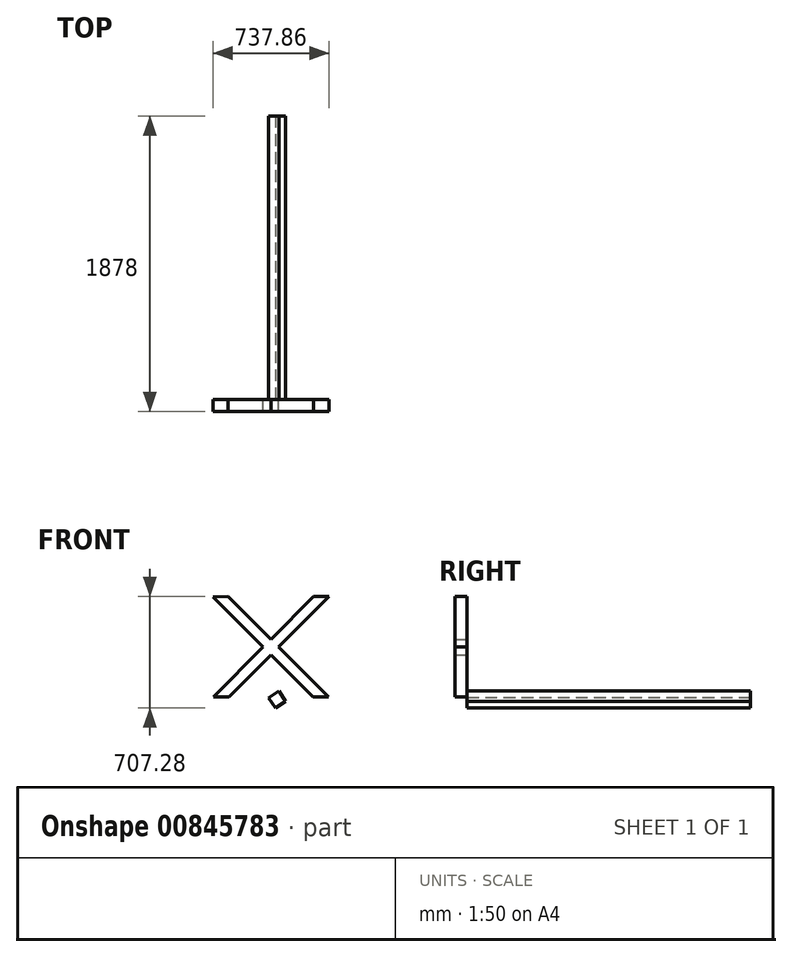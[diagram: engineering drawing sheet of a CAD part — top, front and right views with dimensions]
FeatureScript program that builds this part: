
annotation { "Feature Type Name" : "Feature", "Feature Type Description" : "" }
export const myFeature = defineFeature(function(context is Context, id is Id, definition is map)
    precondition{}
    {
        {
            var Q0;
            Q0=qCreatedBy(makeId("Front.planeOp"),FACE);
            var sketch = newSketch(context, id + "F0", { "sketchPlane" : qUnion([Q0])});
            skLineSegment(sketch, "E0.left", {"start": v(-20.76, 27.69) * mm, "end": v(-657.15, 664.08) * mm});
            skLineSegment(sketch, "E0.right", {"start": v(76.5, 27.58) * mm, "end": v(-560.07, 664.16) * mm});
            skLineSegment(sketch, "E1.MirrorCS", {"start": v(-652.73, 28.4) * mm, "end": v(-16.55, 664.6) * mm});
            skLineSegment(sketch, "E2.MirrorCS", {"start": v(-555.68, 28.29) * mm, "end": v(80.71, 664.68) * mm});
            skPoint(sketch, "E3", {"position": v(-287.7, 348.45) * mm});
            skLineSegment(sketch, "E4", {"start": v(-657.15, 664.08) * mm, "end": v(-560.07, 664.16) * mm});
            skLineSegment(sketch, "E5.trimOffspring", {"start": v(-16.55, 664.6) * mm, "end": v(80.71, 664.68) * mm});
            skLineSegment(sketch, "E6", {"start": v(-652.73, 28.4) * mm, "end": v(-555.68, 28.29) * mm});
            skLineSegment(sketch, "E7.trimOffspring", {"start": v(-20.76, 27.69) * mm, "end": v(76.5, 27.58) * mm});
            skSolve(sketch);
        }
        {
            var Q0;
            {var subQ0=sQuery(id+"F0.wireOp",EDGE,"E4");Q0=makeQuery(id+"F0.imprint","IMPRINT",FACE,{"disambiguationData":[TD([[makeQuery(id+"F0.imprint","IMPRINT",EDGE,{"derivedFrom":subQ0}),-1.0]])]});}
            var Q1;
            {var subQ5=sQuery(id+"F0.wireOp",EDGE,"E5.trimOffspring");Q1=makeQuery(id+"F0.imprint","IMPRINT",FACE,{"disambiguationData":[TD([[makeQuery(id+"F0.imprint","IMPRINT",EDGE,{"derivedFrom":subQ5}),-1.0]])]});}
            var Q2;
            {var subQ0=sQuery(id+"F0.wireOp",EDGE,"E2.MirrorCS");var subQ1=sQuery(id+"F0.wireOp",EDGE,"E0.left");var subQ2=makeQuery(id+"F0.imprint","INTERSECT",VERTEX,{"derivedFrom":[subQ1,subQ0]});Q2=makeQuery(id+"F0.imprint","IMPRINT",FACE,{"disambiguationData":[TD([[makeQuery(id+"F0.imprint","IMPRINT",EDGE,{"disambiguationData":[TD([[subQ2,-1.0]])],"derivedFrom":subQ1}),-1.0]])]});}
            var Q3;
            {var subQ0=sQuery(id+"F0.wireOp",EDGE,"E7.trimOffspring");Q3=makeQuery(id+"F0.imprint","IMPRINT",FACE,{"disambiguationData":[TD([[makeQuery(id+"F0.imprint","IMPRINT",EDGE,{"derivedFrom":subQ0}),1.0]])]});}
            var Q4;
            {var subQ5=sQuery(id+"F0.wireOp",EDGE,"E6");Q4=makeQuery(id+"F0.imprint","IMPRINT",FACE,{"disambiguationData":[TD([[makeQuery(id+"F0.imprint","IMPRINT",EDGE,{"derivedFrom":subQ5}),1.0]])]});}
            extrude(context, id + "F1", {"entities" : qUnion([Q0, Q1, Q2, Q3, Q4]), "depth" : 78 * mm, "offsetDistance" : 25 * mm});
        }
        {
            var Q0;
            Q0=qCreatedBy(makeId("Front.planeOp"),FACE);
            var sketch = newSketch(context, id + "F2", { "sketchPlane" : qUnion([Q0])});
            skLineSegment(sketch, "E8", {"start": v(-301.94, 22.74) * mm, "end": v(-259.35, -42.6) * mm});
            skLineSegment(sketch, "E9", {"start": v(-259.35, -42.6) * mm, "end": v(-194, 0) * mm});
            skLineSegment(sketch, "E10", {"start": v(-194, 0) * mm, "end": v(-236.6, 65.34) * mm});
            skLineSegment(sketch, "E11", {"start": v(-236.6, 65.34) * mm, "end": v(-301.94, 22.74) * mm});
            skSolve(sketch);
        }
        {
            var Q0;
            Q0=makeQuery(id+"F2.imprint","IMPRINT",FACE,{"disambiguationData":[TD([[makeQuery(id+"F2.imprint","IMPRINT",EDGE,{"derivedFrom":sQuery(id+"F2.wireOp",EDGE,"E8")}),1.0]])]});
            extrude(context, id + "F3", {"entities" : qUnion([Q0]), "oppositeDirection" : true, "depth" : 1800 * mm, "offsetDistance" : 25 * mm});
        }
    });
